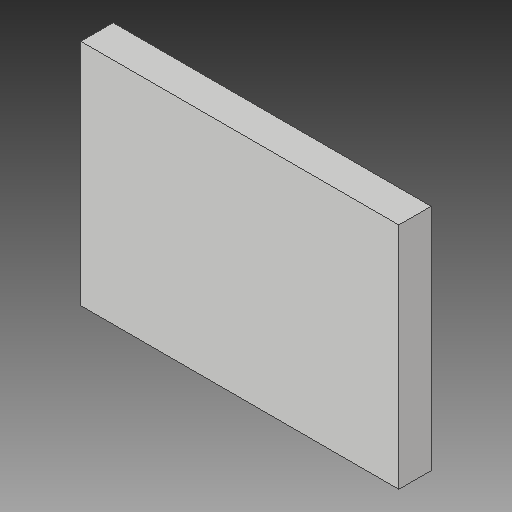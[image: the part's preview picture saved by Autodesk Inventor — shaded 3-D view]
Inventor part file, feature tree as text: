
AUTODESK INVENTOR PART (.ipt)
format: ipt  version: 2018 (Build 220112000, 112)  size: 90,112 bytes
history: native  units: mm
features: other x1, extrude x1, sketch x1
ambient origin geometry x8: Origin, YZ Plane, XZ Plane, XY Plane, X Axis, Y Axis, Z Axis, Center Point
bodies: Body1 (feature_tree)
feature tree (3):
  other  "Sólido1"
  extrude  "Extrusão1"  Depth=90.0mm
  sketch  "Esboço1"  dims[d0=125.0mm d1=90.0mm d2=12.7mm d3=0.0mm]
